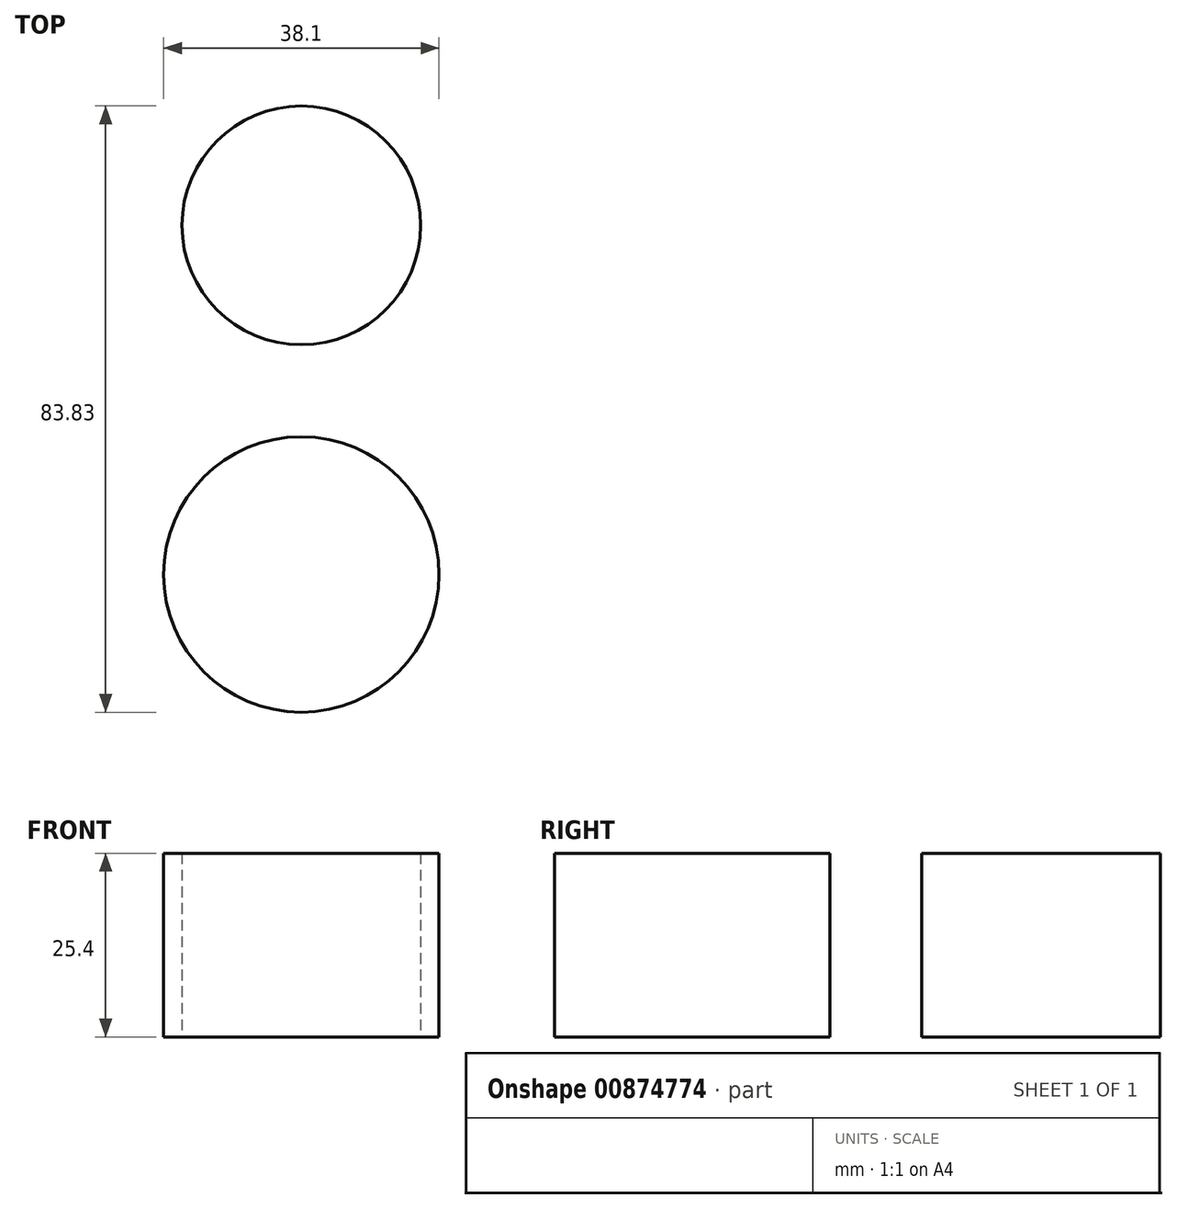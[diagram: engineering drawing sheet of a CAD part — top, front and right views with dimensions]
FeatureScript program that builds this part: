
annotation { "Feature Type Name" : "Feature", "Feature Type Description" : "" }
export const myFeature = defineFeature(function(context is Context, id is Id, definition is map)
    precondition{}
    {
        {
            var Q0;
            Q0=qCreatedBy(makeId("Top.planeOp"),FACE);
            var sketch = newSketch(context, id + "F0", { "sketchPlane" : qUnion([Q0])});
            skLineSegment(sketch, "E0", {"start": v(-18.02, 16.33) * mm, "end": v(-16.3, 15.16) * mm});
            skCircle(sketch, "E1", {"center": v(0, 0) * mm, "radius": 19.05 * mm});
            skLineSegment(sketch, "E2", {"start": v(0, 19.05) * mm, "end": v(0, 48.27) * mm});
            skCircle(sketch, "E3", {"center": v(0, 48.27) * mm, "radius": 16.51 * mm});
            skLineSegment(sketch, "E4", {"start": v(0, 19.05) * mm, "end": v(0, 0) * mm});
            skLineSegment(sketch, "E5", {"start": v(77.16, -76.76) * mm, "end": v(75.88, -75.48) * mm});
            skSolve(sketch);
        }
        {
            var Q0;
            Q0 = qSketchRegion(id + "F0", true);
            extrude(context, id + "F1", {"entities" : qUnion([Q0]), "depth" : 25.4 * mm, "offsetDistance" : 25.4 * mm});
        }
    });
